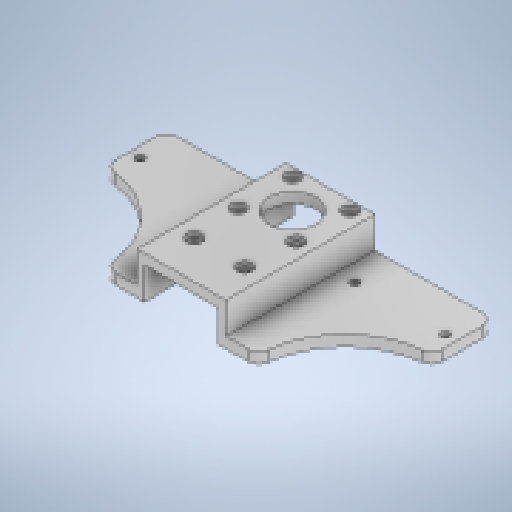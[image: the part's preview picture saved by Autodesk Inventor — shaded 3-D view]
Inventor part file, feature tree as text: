
AUTODESK INVENTOR PART (.ipt)
format: ipt  version: 2024.2 (Build 282272000, 272)  size: 365,056 bytes
history: native  units: in
note: dims shown in document units (in); Inventor stores cm internally (conversion verified against a paired STEP export)
features: sketch x5, projected_geometry x3, extrude x1, mirror x1, fillet x1, plane x1
ambient origin geometry x8: Origin, YZ Plane, XZ Plane, XY Plane, X Axis, Y Axis, Z Axis, Center Point
bodies: Solid1 (feature_tree)
feature tree (12):
  extrude  "Extrusion1"  Depth=0.1122in
  mirror  "Mirror1"
  fillet  "Fillet3"  Radius=0.2283in
  sketch  "Sketch1"  dims[d0=0.8067in d1=0.1122in d3=0.2283in]
  sketch  "Sketch8"  dims[d4=0.1181in]
  projected_geometry  "Projected Loop3"
  sketch  "Sketch9"  dims[d5=0.1181in]
  projected_geometry  "Projected Loop5"
  plane  "Work Plane1"
  sketch  "Sketch10"  dims[d6=1.378in]
  projected_geometry  "Projected Loop6"
  sketch  "Sketch11"  dims[d7=1.378in d11=1.6181in d12=0.0in d42=0.1181in d43=0.9843in d44=0.0968in d45=0.2362in d46=0.1575in d47=0.0787in d48=90.0deg d49=0.315in d50=0.8108in d51=0.4114in d53=0.1181in d60=0.9449in d61=0.3937in d62=0.0in d73=1.2992in d74=1.2992in d75=0.5118in d76=0.4133in d77=0.3937in d78=0.0in d86=0.0827in d87=0.2362in d88=0.1614in d89=0.0551in d90=90.0deg d91=0.315in d92=0.8108in d125=0.1181in d63=0.0059in d64=0.0098in d65=0.0148in d66=0.5635in d67=0.0295in d68=0.8108in d69=0.0025in d70=0.0295in d71=0.0148in]
